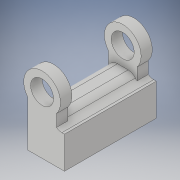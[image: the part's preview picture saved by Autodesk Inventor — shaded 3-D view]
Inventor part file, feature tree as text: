
AUTODESK INVENTOR PART (.ipt)
format: ipt  version: 2019 (Build 230136000, 136)  size: 284,160 bytes
history: native  units: in
note: dims shown in document units (in); Inventor stores cm internally (conversion verified against a paired STEP export)
features: sketch x9, fillet x9, extrude x7
ambient origin geometry x8: Origin, YZ Plane, XZ Plane, XY Plane, X Axis, Y Axis, Z Axis, Center Point
bodies: Solid1 (feature_tree)
feature tree (25):
  extrude  "Extrusion1"  Depth=0.1969in
  sketch  "3D Sketch1"
  sketch  "Sketch2"  dims[d5=0.3937in d6=0.7874in d7=0.0in]
  extrude  "Extrusion2"  Depth=0.7874in TaperAngle=0.0deg
  extrude  "Extrusion3"  Depth=0.0039in TaperAngle=0.0deg
  extrude  "Extrusion4"  Depth=0.5935in
  fillet  "Fillet1"  Radius=0.3937in
  fillet  "Fillet2"  Radius=0.2756in
  extrude  "Extrusion5"  Depth=0.315in
  sketch  "Sketch7"  dims[d27=0.3937in d28=0.0in d30=0.1575in d31=0.1575in d32=0.1969in d33=0.0in d34=0.1969in d35=0.0in d36=0.0787in d37=0.0787in d39=0.0787in d40=0.0787in]
  sketch  "Sketch8"  dims[d44=0.0787in d45=0.0787in d46=0.0787in]
  extrude  "Extrusion6"  Depth=0.0787in
  extrude  "Extrusion7"  Depth=0.1575in
  fillet  "Fillet3"  Radius=0.1575in
  fillet  "Fillet4"  Radius=0.1969in
  fillet  "Fillet6"  Radius=0.1969in
  fillet  "Fillet7"  Radius=0.0787in
  fillet  "Fillet11"  Radius=0.0787in
  fillet  "Fillet12"  Radius=0.0787in
  fillet  "Fillet13"  Radius=0.0787in
  sketch  "Sketch1"  dims[d2=0.315in d3=0.1969in]
  sketch  "Sketch3"  dims[d8=0.7874in d9=0.0in d10=0.0039in d11=0.0in]
  sketch  "Sketch4"  dims[d12=0.315in d13=0.5935in d14=0.3937in d15=0.0in d17=0.2756in]
  sketch  "Sketch5"  dims[d18=0.1181in d19=0.315in]
  sketch  "Sketch6"  dims[d23=0.0787in d24=0.0787in]
